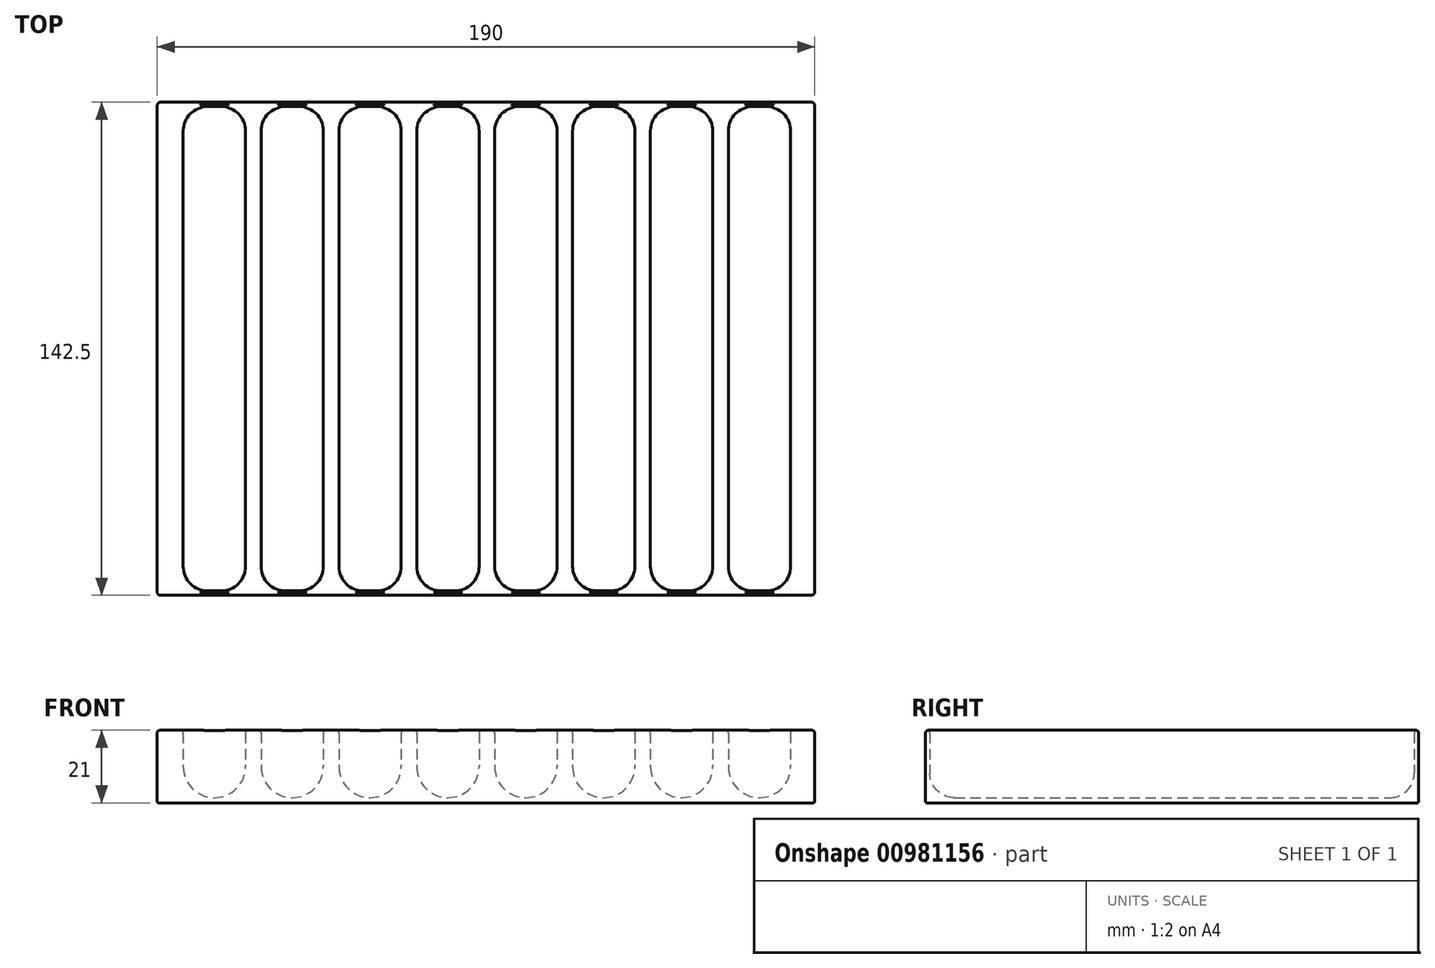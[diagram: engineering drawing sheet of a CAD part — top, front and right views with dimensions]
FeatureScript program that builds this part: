
annotation { "Feature Type Name" : "Feature", "Feature Type Description" : "" }
export const myFeature = defineFeature(function(context is Context, id is Id, definition is map)
    precondition{}
    {
        {
            var Q0;
            Q0=qCreatedBy(makeId("Top.planeOp"),FACE);
            var sketch = newSketch(context, id + "F0", { "sketchPlane" : qUnion([Q0])});
            skLineSegment(sketch, "E0.bottom", {"start": v(95, -71.25) * mm, "end": v(-95, -71.25) * mm});
            skLineSegment(sketch, "E0.top", {"start": v(95, 71.25) * mm, "end": v(-95, 71.25) * mm});
            skLineSegment(sketch, "E0.left", {"start": v(95, -71.25) * mm, "end": v(95, 71.25) * mm});
            skLineSegment(sketch, "E0.right", {"start": v(-95, -71.25) * mm, "end": v(-95, 71.25) * mm});
            skPoint(sketch, "E0.middle", {"position": v(0, 0) * mm});
            skSolve(sketch);
        }
        {
            var Q0;
            Q0 = qSketchRegion(id + "F0", true);
            extrude(context, id + "F1", {"entities" : qUnion([Q0]), "depth" : 21 * mm, "offsetDistance" : 25 * mm});
        }
        {
            var Q0;
            Q0=qCreatedBy(makeId("Front.planeOp"),FACE);
            var sketch = newSketch(context, id + "F2", { "sketchPlane" : qUnion([Q0])});
            skLineSegment(sketch, "E1.bottom", {"start": v(-69.47, 26.52) * mm, "end": v(-87.47, 26.52) * mm});
            skLineSegment(sketch, "E1.top", {"start": v(-69.47, 10.52) * mm, "end": v(-87.47, 10.52) * mm});
            skLineSegment(sketch, "E1.left", {"start": v(-69.47, 26.52) * mm, "end": v(-69.47, 10.52) * mm});
            skLineSegment(sketch, "E1.right", {"start": v(-87.47, 26.52) * mm, "end": v(-87.47, 10.52) * mm});
            skPoint(sketch, "E1.middle", {"position": v(-78.47, 18.52) * mm});
            skArc(sketch, "E2", {"start": v(-87.47, 10.52) * mm, "mid": v(-78.47, 1.52) * mm, "end": v(-69.47, 10.52) * mm});
            skSolve(sketch);
        }
        {
            var Q0;
            Q0=makeQuery(id+"F2.imprint","IMPRINT",FACE,{"disambiguationData":[TD([[makeQuery(id+"F2.imprint","IMPRINT",EDGE,{"derivedFrom":sQuery(id+"F2.wireOp",EDGE,"E1.bottom")}),1.0]])]});
            var Q1;
            Q1=makeQuery(id+"F2.imprint","IMPRINT",FACE,{"disambiguationData":[TD([[makeQuery(id+"F2.imprint","IMPRINT",EDGE,{"derivedFrom":sQuery(id+"F2.wireOp",EDGE,"E1.top")}),1.0]])]});
            extrude(context, id + "F3", {"entities" : qUnion([Q0, Q1]), "depth" : 140 * mm, "offsetDistance" : 25 * mm, "symmetric" : true});
        }
        {
            var Q0;
            Q0=makeQuery(id+"F3.opExtrude","SWEPT_BODY",BODY,{"disambiguationData":[OSD([sQuery(id+"F2.wireOp",EDGE,"E1.bottom"),sQuery(id+"F2.wireOp",EDGE,"E1.left"),sQuery(id+"F2.wireOp",EDGE,"E1.right"),sQuery(id+"F2.wireOp",EDGE,"E2")])]});
            transform(context, id + "F4", {"entities" : qUnion([Q0]), "transformType" : TransformType.TRANSLATION_3D, "dx" : 22.5 * mm, "dy" : 0 * mm, "dz" : 0 * mm, "makeCopy" : true});
        }
        {
            var Q0;
            Q0=makeQuery(id+"F4.opPattern","COPY",BODY,{"derivedFrom":makeQuery(id+"F3.opExtrude","SWEPT_BODY",BODY,{"disambiguationData":[OSD([sQuery(id+"F2.wireOp",EDGE,"E1.bottom"),sQuery(id+"F2.wireOp",EDGE,"E1.left"),sQuery(id+"F2.wireOp",EDGE,"E1.right"),sQuery(id+"F2.wireOp",EDGE,"E2")])]}),"instanceName":"1"});
            transform(context, id + "F5", {"entities" : qUnion([Q0]), "transformType" : TransformType.TRANSLATION_3D, "dx" : 22.5 * mm, "dy" : 0 * mm, "dz" : 0 * mm, "makeCopy" : true});
        }
        {
            var Q0;
            Q0=makeQuery(id+"F5.opPattern","COPY",BODY,{"derivedFrom":makeQuery(id+"F4.opPattern","COPY",BODY,{"derivedFrom":makeQuery(id+"F3.opExtrude","SWEPT_BODY",BODY,{"disambiguationData":[OSD([sQuery(id+"F2.wireOp",EDGE,"E1.bottom"),sQuery(id+"F2.wireOp",EDGE,"E1.left"),sQuery(id+"F2.wireOp",EDGE,"E1.right"),sQuery(id+"F2.wireOp",EDGE,"E2")])]}),"instanceName":"1"}),"instanceName":"1"});
            transform(context, id + "F6", {"entities" : qUnion([Q0]), "transformType" : TransformType.TRANSLATION_3D, "dx" : 22.5 * mm, "dy" : 0 * mm, "dz" : 0 * mm, "makeCopy" : true});
        }
        {
            var Q0;
            Q0=makeQuery(id+"F6.opPattern","COPY",BODY,{"derivedFrom":makeQuery(id+"F5.opPattern","COPY",BODY,{"derivedFrom":makeQuery(id+"F4.opPattern","COPY",BODY,{"derivedFrom":makeQuery(id+"F3.opExtrude","SWEPT_BODY",BODY,{"disambiguationData":[OSD([sQuery(id+"F2.wireOp",EDGE,"E1.bottom"),sQuery(id+"F2.wireOp",EDGE,"E1.left"),sQuery(id+"F2.wireOp",EDGE,"E1.right"),sQuery(id+"F2.wireOp",EDGE,"E2")])]}),"instanceName":"1"}),"instanceName":"1"}),"instanceName":"1"});
            transform(context, id + "F7", {"entities" : qUnion([Q0]), "transformType" : TransformType.TRANSLATION_3D, "dx" : 22.5 * mm, "dy" : 0 * mm, "dz" : 0 * mm, "makeCopy" : true});
        }
        {
            var Q0;
            Q0=makeQuery(id+"F7.opPattern","COPY",BODY,{"derivedFrom":makeQuery(id+"F6.opPattern","COPY",BODY,{"derivedFrom":makeQuery(id+"F5.opPattern","COPY",BODY,{"derivedFrom":makeQuery(id+"F4.opPattern","COPY",BODY,{"derivedFrom":makeQuery(id+"F3.opExtrude","SWEPT_BODY",BODY,{"disambiguationData":[OSD([sQuery(id+"F2.wireOp",EDGE,"E1.bottom"),sQuery(id+"F2.wireOp",EDGE,"E1.left"),sQuery(id+"F2.wireOp",EDGE,"E1.right"),sQuery(id+"F2.wireOp",EDGE,"E2")])]}),"instanceName":"1"}),"instanceName":"1"}),"instanceName":"1"}),"instanceName":"1"});
            transform(context, id + "F8", {"entities" : qUnion([Q0]), "transformType" : TransformType.TRANSLATION_3D, "dx" : 22.5 * mm, "dy" : 0 * mm, "dz" : 0 * mm, "makeCopy" : true});
        }
        {
            var Q0;
            Q0=makeQuery(id+"F8.opPattern","COPY",BODY,{"derivedFrom":makeQuery(id+"F7.opPattern","COPY",BODY,{"derivedFrom":makeQuery(id+"F6.opPattern","COPY",BODY,{"derivedFrom":makeQuery(id+"F5.opPattern","COPY",BODY,{"derivedFrom":makeQuery(id+"F4.opPattern","COPY",BODY,{"derivedFrom":makeQuery(id+"F3.opExtrude","SWEPT_BODY",BODY,{"disambiguationData":[OSD([sQuery(id+"F2.wireOp",EDGE,"E1.bottom"),sQuery(id+"F2.wireOp",EDGE,"E1.left"),sQuery(id+"F2.wireOp",EDGE,"E1.right"),sQuery(id+"F2.wireOp",EDGE,"E2")])]}),"instanceName":"1"}),"instanceName":"1"}),"instanceName":"1"}),"instanceName":"1"}),"instanceName":"1"});
            transform(context, id + "F9", {"entities" : qUnion([Q0]), "transformType" : TransformType.TRANSLATION_3D, "dx" : 22.5 * mm, "dy" : 0 * mm, "dz" : 0 * mm, "makeCopy" : true});
        }
        {
            var Q0;
            Q0=makeQuery(id+"F9.opPattern","COPY",BODY,{"derivedFrom":makeQuery(id+"F8.opPattern","COPY",BODY,{"derivedFrom":makeQuery(id+"F7.opPattern","COPY",BODY,{"derivedFrom":makeQuery(id+"F6.opPattern","COPY",BODY,{"derivedFrom":makeQuery(id+"F5.opPattern","COPY",BODY,{"derivedFrom":makeQuery(id+"F4.opPattern","COPY",BODY,{"derivedFrom":makeQuery(id+"F3.opExtrude","SWEPT_BODY",BODY,{"disambiguationData":[OSD([sQuery(id+"F2.wireOp",EDGE,"E1.bottom"),sQuery(id+"F2.wireOp",EDGE,"E1.left"),sQuery(id+"F2.wireOp",EDGE,"E1.right"),sQuery(id+"F2.wireOp",EDGE,"E2")])]}),"instanceName":"1"}),"instanceName":"1"}),"instanceName":"1"}),"instanceName":"1"}),"instanceName":"1"}),"instanceName":"1"});
            transform(context, id + "F10", {"entities" : qUnion([Q0]), "transformType" : TransformType.TRANSLATION_3D, "dx" : 22.5 * mm, "dy" : 0 * mm, "dz" : 0 * mm, "makeCopy" : true});
        }
        {
            var Q0;
            Q0=makeQuery(id+"F3.opExtrude","SWEPT_BODY",BODY,{"disambiguationData":[OSD([sQuery(id+"F2.wireOp",EDGE,"E1.bottom"),sQuery(id+"F2.wireOp",EDGE,"E1.left"),sQuery(id+"F2.wireOp",EDGE,"E1.right"),sQuery(id+"F2.wireOp",EDGE,"E2")])]});
            var Q1;
            Q1=makeQuery(id+"F4.opPattern","COPY",BODY,{"derivedFrom":makeQuery(id+"F3.opExtrude","SWEPT_BODY",BODY,{"disambiguationData":[OSD([sQuery(id+"F2.wireOp",EDGE,"E1.bottom"),sQuery(id+"F2.wireOp",EDGE,"E1.left"),sQuery(id+"F2.wireOp",EDGE,"E1.right"),sQuery(id+"F2.wireOp",EDGE,"E2")])]}),"instanceName":"1"});
            var Q2;
            Q2=makeQuery(id+"F5.opPattern","COPY",BODY,{"derivedFrom":makeQuery(id+"F4.opPattern","COPY",BODY,{"derivedFrom":makeQuery(id+"F3.opExtrude","SWEPT_BODY",BODY,{"disambiguationData":[OSD([sQuery(id+"F2.wireOp",EDGE,"E1.bottom"),sQuery(id+"F2.wireOp",EDGE,"E1.left"),sQuery(id+"F2.wireOp",EDGE,"E1.right"),sQuery(id+"F2.wireOp",EDGE,"E2")])]}),"instanceName":"1"}),"instanceName":"1"});
            var Q3;
            Q3=makeQuery(id+"F6.opPattern","COPY",BODY,{"derivedFrom":makeQuery(id+"F5.opPattern","COPY",BODY,{"derivedFrom":makeQuery(id+"F4.opPattern","COPY",BODY,{"derivedFrom":makeQuery(id+"F3.opExtrude","SWEPT_BODY",BODY,{"disambiguationData":[OSD([sQuery(id+"F2.wireOp",EDGE,"E1.bottom"),sQuery(id+"F2.wireOp",EDGE,"E1.left"),sQuery(id+"F2.wireOp",EDGE,"E1.right"),sQuery(id+"F2.wireOp",EDGE,"E2")])]}),"instanceName":"1"}),"instanceName":"1"}),"instanceName":"1"});
            var Q4;
            Q4=makeQuery(id+"F7.opPattern","COPY",BODY,{"derivedFrom":makeQuery(id+"F6.opPattern","COPY",BODY,{"derivedFrom":makeQuery(id+"F5.opPattern","COPY",BODY,{"derivedFrom":makeQuery(id+"F4.opPattern","COPY",BODY,{"derivedFrom":makeQuery(id+"F3.opExtrude","SWEPT_BODY",BODY,{"disambiguationData":[OSD([sQuery(id+"F2.wireOp",EDGE,"E1.bottom"),sQuery(id+"F2.wireOp",EDGE,"E1.left"),sQuery(id+"F2.wireOp",EDGE,"E1.right"),sQuery(id+"F2.wireOp",EDGE,"E2")])]}),"instanceName":"1"}),"instanceName":"1"}),"instanceName":"1"}),"instanceName":"1"});
            var Q5;
            Q5=makeQuery(id+"F8.opPattern","COPY",BODY,{"derivedFrom":makeQuery(id+"F7.opPattern","COPY",BODY,{"derivedFrom":makeQuery(id+"F6.opPattern","COPY",BODY,{"derivedFrom":makeQuery(id+"F5.opPattern","COPY",BODY,{"derivedFrom":makeQuery(id+"F4.opPattern","COPY",BODY,{"derivedFrom":makeQuery(id+"F3.opExtrude","SWEPT_BODY",BODY,{"disambiguationData":[OSD([sQuery(id+"F2.wireOp",EDGE,"E1.bottom"),sQuery(id+"F2.wireOp",EDGE,"E1.left"),sQuery(id+"F2.wireOp",EDGE,"E1.right"),sQuery(id+"F2.wireOp",EDGE,"E2")])]}),"instanceName":"1"}),"instanceName":"1"}),"instanceName":"1"}),"instanceName":"1"}),"instanceName":"1"});
            var Q6;
            Q6=makeQuery(id+"F9.opPattern","COPY",BODY,{"derivedFrom":makeQuery(id+"F8.opPattern","COPY",BODY,{"derivedFrom":makeQuery(id+"F7.opPattern","COPY",BODY,{"derivedFrom":makeQuery(id+"F6.opPattern","COPY",BODY,{"derivedFrom":makeQuery(id+"F5.opPattern","COPY",BODY,{"derivedFrom":makeQuery(id+"F4.opPattern","COPY",BODY,{"derivedFrom":makeQuery(id+"F3.opExtrude","SWEPT_BODY",BODY,{"disambiguationData":[OSD([sQuery(id+"F2.wireOp",EDGE,"E1.bottom"),sQuery(id+"F2.wireOp",EDGE,"E1.left"),sQuery(id+"F2.wireOp",EDGE,"E1.right"),sQuery(id+"F2.wireOp",EDGE,"E2")])]}),"instanceName":"1"}),"instanceName":"1"}),"instanceName":"1"}),"instanceName":"1"}),"instanceName":"1"}),"instanceName":"1"});
            var Q7;
            Q7=makeQuery(id+"F10.opPattern","COPY",BODY,{"derivedFrom":makeQuery(id+"F9.opPattern","COPY",BODY,{"derivedFrom":makeQuery(id+"F8.opPattern","COPY",BODY,{"derivedFrom":makeQuery(id+"F7.opPattern","COPY",BODY,{"derivedFrom":makeQuery(id+"F6.opPattern","COPY",BODY,{"derivedFrom":makeQuery(id+"F5.opPattern","COPY",BODY,{"derivedFrom":makeQuery(id+"F4.opPattern","COPY",BODY,{"derivedFrom":makeQuery(id+"F3.opExtrude","SWEPT_BODY",BODY,{"disambiguationData":[OSD([sQuery(id+"F2.wireOp",EDGE,"E1.bottom"),sQuery(id+"F2.wireOp",EDGE,"E1.left"),sQuery(id+"F2.wireOp",EDGE,"E1.right"),sQuery(id+"F2.wireOp",EDGE,"E2")])]}),"instanceName":"1"}),"instanceName":"1"}),"instanceName":"1"}),"instanceName":"1"}),"instanceName":"1"}),"instanceName":"1"}),"instanceName":"1"});
            var Q8;
            Q8=makeQuery(id+"F1.opExtrude","SWEPT_BODY",BODY,{"disambiguationData":[OSD([sQuery(id+"F0.wireOp",EDGE,"E0.bottom"),sQuery(id+"F0.wireOp",EDGE,"E0.top"),sQuery(id+"F0.wireOp",EDGE,"E0.left"),sQuery(id+"F0.wireOp",EDGE,"E0.right")])]});
            booleanBodies(context, id + "F11", {"operationType" : BooleanOperationType.SUBTRACTION, "tools" : qUnion([Q0, Q1, Q2, Q3, Q4, Q5, Q6, Q7]), "targets" : qUnion([Q8])});
        }
        {
            var Q0;
            Q0=makeQuery(id+"F11.opBoolean","COPY",EDGE,{"derivedFrom":makeQuery(id+"F3.opExtrude","CAP_EDGE",EDGE,{"disambiguationData":[OSD([sQuery(id+"F2.wireOp",EDGE,"E2")])],"isStart":true})});
            var Q1;
            Q1=makeQuery(id+"F11.opBoolean","COPY",EDGE,{"derivedFrom":makeQuery(id+"F4.opPattern","COPY",EDGE,{"derivedFrom":makeQuery(id+"F3.opExtrude","CAP_EDGE",EDGE,{"disambiguationData":[OSD([sQuery(id+"F2.wireOp",EDGE,"E2")])],"isStart":true}),"instanceName":"1"})});
            var Q2;
            Q2=makeQuery(id+"F11.opBoolean","COPY",EDGE,{"derivedFrom":makeQuery(id+"F5.opPattern","COPY",EDGE,{"derivedFrom":makeQuery(id+"F4.opPattern","COPY",EDGE,{"derivedFrom":makeQuery(id+"F3.opExtrude","CAP_EDGE",EDGE,{"disambiguationData":[OSD([sQuery(id+"F2.wireOp",EDGE,"E2")])],"isStart":true}),"instanceName":"1"}),"instanceName":"1"})});
            var Q3;
            Q3=makeQuery(id+"F11.opBoolean","COPY",EDGE,{"derivedFrom":makeQuery(id+"F6.opPattern","COPY",EDGE,{"derivedFrom":makeQuery(id+"F5.opPattern","COPY",EDGE,{"derivedFrom":makeQuery(id+"F4.opPattern","COPY",EDGE,{"derivedFrom":makeQuery(id+"F3.opExtrude","CAP_EDGE",EDGE,{"disambiguationData":[OSD([sQuery(id+"F2.wireOp",EDGE,"E2")])],"isStart":true}),"instanceName":"1"}),"instanceName":"1"}),"instanceName":"1"})});
            var Q4;
            Q4=makeQuery(id+"F11.opBoolean","COPY",EDGE,{"derivedFrom":makeQuery(id+"F8.opPattern","COPY",EDGE,{"derivedFrom":makeQuery(id+"F7.opPattern","COPY",EDGE,{"derivedFrom":makeQuery(id+"F6.opPattern","COPY",EDGE,{"derivedFrom":makeQuery(id+"F5.opPattern","COPY",EDGE,{"derivedFrom":makeQuery(id+"F4.opPattern","COPY",EDGE,{"derivedFrom":makeQuery(id+"F3.opExtrude","CAP_EDGE",EDGE,{"disambiguationData":[OSD([sQuery(id+"F2.wireOp",EDGE,"E2")])],"isStart":true}),"instanceName":"1"}),"instanceName":"1"}),"instanceName":"1"}),"instanceName":"1"}),"instanceName":"1"})});
            var Q5;
            Q5=makeQuery(id+"F11.opBoolean","COPY",EDGE,{"derivedFrom":makeQuery(id+"F7.opPattern","COPY",EDGE,{"derivedFrom":makeQuery(id+"F6.opPattern","COPY",EDGE,{"derivedFrom":makeQuery(id+"F5.opPattern","COPY",EDGE,{"derivedFrom":makeQuery(id+"F4.opPattern","COPY",EDGE,{"derivedFrom":makeQuery(id+"F3.opExtrude","CAP_EDGE",EDGE,{"disambiguationData":[OSD([sQuery(id+"F2.wireOp",EDGE,"E2")])],"isStart":true}),"instanceName":"1"}),"instanceName":"1"}),"instanceName":"1"}),"instanceName":"1"})});
            var Q6;
            Q6=makeQuery(id+"F11.opBoolean","COPY",EDGE,{"derivedFrom":makeQuery(id+"F9.opPattern","COPY",EDGE,{"derivedFrom":makeQuery(id+"F8.opPattern","COPY",EDGE,{"derivedFrom":makeQuery(id+"F7.opPattern","COPY",EDGE,{"derivedFrom":makeQuery(id+"F6.opPattern","COPY",EDGE,{"derivedFrom":makeQuery(id+"F5.opPattern","COPY",EDGE,{"derivedFrom":makeQuery(id+"F4.opPattern","COPY",EDGE,{"derivedFrom":makeQuery(id+"F3.opExtrude","CAP_EDGE",EDGE,{"disambiguationData":[OSD([sQuery(id+"F2.wireOp",EDGE,"E2")])],"isStart":true}),"instanceName":"1"}),"instanceName":"1"}),"instanceName":"1"}),"instanceName":"1"}),"instanceName":"1"}),"instanceName":"1"})});
            var Q7;
            Q7=makeQuery(id+"F11.opBoolean","COPY",EDGE,{"derivedFrom":makeQuery(id+"F10.opPattern","COPY",EDGE,{"derivedFrom":makeQuery(id+"F9.opPattern","COPY",EDGE,{"derivedFrom":makeQuery(id+"F8.opPattern","COPY",EDGE,{"derivedFrom":makeQuery(id+"F7.opPattern","COPY",EDGE,{"derivedFrom":makeQuery(id+"F6.opPattern","COPY",EDGE,{"derivedFrom":makeQuery(id+"F5.opPattern","COPY",EDGE,{"derivedFrom":makeQuery(id+"F4.opPattern","COPY",EDGE,{"derivedFrom":makeQuery(id+"F3.opExtrude","CAP_EDGE",EDGE,{"disambiguationData":[OSD([sQuery(id+"F2.wireOp",EDGE,"E2")])],"isStart":true}),"instanceName":"1"}),"instanceName":"1"}),"instanceName":"1"}),"instanceName":"1"}),"instanceName":"1"}),"instanceName":"1"}),"instanceName":"1"})});
            var Q8;
            Q8=makeQuery(id+"F11.opBoolean","COPY",EDGE,{"derivedFrom":makeQuery(id+"F10.opPattern","COPY",EDGE,{"derivedFrom":makeQuery(id+"F9.opPattern","COPY",EDGE,{"derivedFrom":makeQuery(id+"F8.opPattern","COPY",EDGE,{"derivedFrom":makeQuery(id+"F7.opPattern","COPY",EDGE,{"derivedFrom":makeQuery(id+"F6.opPattern","COPY",EDGE,{"derivedFrom":makeQuery(id+"F5.opPattern","COPY",EDGE,{"derivedFrom":makeQuery(id+"F4.opPattern","COPY",EDGE,{"derivedFrom":makeQuery(id+"F3.opExtrude","CAP_EDGE",EDGE,{"disambiguationData":[OSD([sQuery(id+"F2.wireOp",EDGE,"E2")])],"isStart":false}),"instanceName":"1"}),"instanceName":"1"}),"instanceName":"1"}),"instanceName":"1"}),"instanceName":"1"}),"instanceName":"1"}),"instanceName":"1"})});
            var Q9;
            Q9=makeQuery(id+"F11.opBoolean","COPY",EDGE,{"derivedFrom":makeQuery(id+"F9.opPattern","COPY",EDGE,{"derivedFrom":makeQuery(id+"F8.opPattern","COPY",EDGE,{"derivedFrom":makeQuery(id+"F7.opPattern","COPY",EDGE,{"derivedFrom":makeQuery(id+"F6.opPattern","COPY",EDGE,{"derivedFrom":makeQuery(id+"F5.opPattern","COPY",EDGE,{"derivedFrom":makeQuery(id+"F4.opPattern","COPY",EDGE,{"derivedFrom":makeQuery(id+"F3.opExtrude","CAP_EDGE",EDGE,{"disambiguationData":[OSD([sQuery(id+"F2.wireOp",EDGE,"E2")])],"isStart":false}),"instanceName":"1"}),"instanceName":"1"}),"instanceName":"1"}),"instanceName":"1"}),"instanceName":"1"}),"instanceName":"1"})});
            var Q10;
            Q10=makeQuery(id+"F11.opBoolean","COPY",EDGE,{"derivedFrom":makeQuery(id+"F8.opPattern","COPY",EDGE,{"derivedFrom":makeQuery(id+"F7.opPattern","COPY",EDGE,{"derivedFrom":makeQuery(id+"F6.opPattern","COPY",EDGE,{"derivedFrom":makeQuery(id+"F5.opPattern","COPY",EDGE,{"derivedFrom":makeQuery(id+"F4.opPattern","COPY",EDGE,{"derivedFrom":makeQuery(id+"F3.opExtrude","CAP_EDGE",EDGE,{"disambiguationData":[OSD([sQuery(id+"F2.wireOp",EDGE,"E2")])],"isStart":false}),"instanceName":"1"}),"instanceName":"1"}),"instanceName":"1"}),"instanceName":"1"}),"instanceName":"1"})});
            var Q11;
            Q11=makeQuery(id+"F11.opBoolean","COPY",EDGE,{"derivedFrom":makeQuery(id+"F7.opPattern","COPY",EDGE,{"derivedFrom":makeQuery(id+"F6.opPattern","COPY",EDGE,{"derivedFrom":makeQuery(id+"F5.opPattern","COPY",EDGE,{"derivedFrom":makeQuery(id+"F4.opPattern","COPY",EDGE,{"derivedFrom":makeQuery(id+"F3.opExtrude","CAP_EDGE",EDGE,{"disambiguationData":[OSD([sQuery(id+"F2.wireOp",EDGE,"E2")])],"isStart":false}),"instanceName":"1"}),"instanceName":"1"}),"instanceName":"1"}),"instanceName":"1"})});
            var Q12;
            Q12=makeQuery(id+"F11.opBoolean","COPY",EDGE,{"derivedFrom":makeQuery(id+"F6.opPattern","COPY",EDGE,{"derivedFrom":makeQuery(id+"F5.opPattern","COPY",EDGE,{"derivedFrom":makeQuery(id+"F4.opPattern","COPY",EDGE,{"derivedFrom":makeQuery(id+"F3.opExtrude","CAP_EDGE",EDGE,{"disambiguationData":[OSD([sQuery(id+"F2.wireOp",EDGE,"E2")])],"isStart":false}),"instanceName":"1"}),"instanceName":"1"}),"instanceName":"1"})});
            var Q13;
            Q13=makeQuery(id+"F11.opBoolean","COPY",EDGE,{"derivedFrom":makeQuery(id+"F5.opPattern","COPY",EDGE,{"derivedFrom":makeQuery(id+"F4.opPattern","COPY",EDGE,{"derivedFrom":makeQuery(id+"F3.opExtrude","CAP_EDGE",EDGE,{"disambiguationData":[OSD([sQuery(id+"F2.wireOp",EDGE,"E2")])],"isStart":false}),"instanceName":"1"}),"instanceName":"1"})});
            var Q14;
            Q14=makeQuery(id+"F11.opBoolean","COPY",EDGE,{"derivedFrom":makeQuery(id+"F4.opPattern","COPY",EDGE,{"derivedFrom":makeQuery(id+"F3.opExtrude","CAP_EDGE",EDGE,{"disambiguationData":[OSD([sQuery(id+"F2.wireOp",EDGE,"E2")])],"isStart":false}),"instanceName":"1"})});
            var Q15;
            Q15=makeQuery(id+"F11.opBoolean","COPY",EDGE,{"derivedFrom":makeQuery(id+"F3.opExtrude","CAP_EDGE",EDGE,{"disambiguationData":[OSD([sQuery(id+"F2.wireOp",EDGE,"E2")])],"isStart":false})});
            fillet(context, id + "F12", {"entities" : qUnion([Q0, Q1, Q2, Q3, Q4, Q5, Q6, Q7, Q8, Q9, Q10, Q11, Q12, Q13, Q14, Q15]), "tangentPropagation" : true, "radius" : 7.1 * mm, "defaultsChanged" : true, "vertexSettings" : [], "allowEdgeOverflow" : false});
        }
        {
            var Q0;
            Q0=makeQuery(id+"F11.opBoolean","INTERSECT",EDGE,{"derivedFrom":[makeQuery(id+"F1.opExtrude","CAP_FACE",FACE,{"disambiguationData":[OSD([sQuery(id+"F0.wireOp",EDGE,"E0.bottom"),sQuery(id+"F0.wireOp",EDGE,"E0.top"),sQuery(id+"F0.wireOp",EDGE,"E0.left"),sQuery(id+"F0.wireOp",EDGE,"E0.right")])],"isStart":false}),makeQuery(id+"F3.opExtrude","SWEPT_FACE",FACE,{"disambiguationData":[OSD([sQuery(id+"F2.wireOp",EDGE,"E1.right")])]})]});
            var Q1;
            Q1=makeQuery(id+"F11.opBoolean","INTERSECT",EDGE,{"derivedFrom":[makeQuery(id+"F1.opExtrude","CAP_FACE",FACE,{"disambiguationData":[OSD([sQuery(id+"F0.wireOp",EDGE,"E0.bottom"),sQuery(id+"F0.wireOp",EDGE,"E0.top"),sQuery(id+"F0.wireOp",EDGE,"E0.left"),sQuery(id+"F0.wireOp",EDGE,"E0.right")])],"isStart":false}),makeQuery(id+"F4.opPattern","COPY",FACE,{"derivedFrom":makeQuery(id+"F3.opExtrude","SWEPT_FACE",FACE,{"disambiguationData":[OSD([sQuery(id+"F2.wireOp",EDGE,"E1.right")])]}),"instanceName":"1"})]});
            var Q2;
            Q2=makeQuery(id+"F11.opBoolean","INTERSECT",EDGE,{"derivedFrom":[makeQuery(id+"F1.opExtrude","CAP_FACE",FACE,{"disambiguationData":[OSD([sQuery(id+"F0.wireOp",EDGE,"E0.bottom"),sQuery(id+"F0.wireOp",EDGE,"E0.top"),sQuery(id+"F0.wireOp",EDGE,"E0.left"),sQuery(id+"F0.wireOp",EDGE,"E0.right")])],"isStart":false}),makeQuery(id+"F5.opPattern","COPY",FACE,{"derivedFrom":makeQuery(id+"F4.opPattern","COPY",FACE,{"derivedFrom":makeQuery(id+"F3.opExtrude","SWEPT_FACE",FACE,{"disambiguationData":[OSD([sQuery(id+"F2.wireOp",EDGE,"E1.right")])]}),"instanceName":"1"}),"instanceName":"1"})]});
            var Q3;
            Q3=makeQuery(id+"F11.opBoolean","INTERSECT",EDGE,{"derivedFrom":[makeQuery(id+"F1.opExtrude","CAP_FACE",FACE,{"disambiguationData":[OSD([sQuery(id+"F0.wireOp",EDGE,"E0.bottom"),sQuery(id+"F0.wireOp",EDGE,"E0.top"),sQuery(id+"F0.wireOp",EDGE,"E0.left"),sQuery(id+"F0.wireOp",EDGE,"E0.right")])],"isStart":false}),makeQuery(id+"F6.opPattern","COPY",FACE,{"derivedFrom":makeQuery(id+"F5.opPattern","COPY",FACE,{"derivedFrom":makeQuery(id+"F4.opPattern","COPY",FACE,{"derivedFrom":makeQuery(id+"F3.opExtrude","SWEPT_FACE",FACE,{"disambiguationData":[OSD([sQuery(id+"F2.wireOp",EDGE,"E1.right")])]}),"instanceName":"1"}),"instanceName":"1"}),"instanceName":"1"})]});
            var Q4;
            Q4=makeQuery(id+"F11.opBoolean","INTERSECT",EDGE,{"derivedFrom":[makeQuery(id+"F1.opExtrude","CAP_FACE",FACE,{"disambiguationData":[OSD([sQuery(id+"F0.wireOp",EDGE,"E0.bottom"),sQuery(id+"F0.wireOp",EDGE,"E0.top"),sQuery(id+"F0.wireOp",EDGE,"E0.left"),sQuery(id+"F0.wireOp",EDGE,"E0.right")])],"isStart":false}),makeQuery(id+"F7.opPattern","COPY",FACE,{"derivedFrom":makeQuery(id+"F6.opPattern","COPY",FACE,{"derivedFrom":makeQuery(id+"F5.opPattern","COPY",FACE,{"derivedFrom":makeQuery(id+"F4.opPattern","COPY",FACE,{"derivedFrom":makeQuery(id+"F3.opExtrude","SWEPT_FACE",FACE,{"disambiguationData":[OSD([sQuery(id+"F2.wireOp",EDGE,"E1.right")])]}),"instanceName":"1"}),"instanceName":"1"}),"instanceName":"1"}),"instanceName":"1"})]});
            var Q5;
            Q5=makeQuery(id+"F11.opBoolean","INTERSECT",EDGE,{"derivedFrom":[makeQuery(id+"F1.opExtrude","CAP_FACE",FACE,{"disambiguationData":[OSD([sQuery(id+"F0.wireOp",EDGE,"E0.bottom"),sQuery(id+"F0.wireOp",EDGE,"E0.top"),sQuery(id+"F0.wireOp",EDGE,"E0.left"),sQuery(id+"F0.wireOp",EDGE,"E0.right")])],"isStart":false}),makeQuery(id+"F8.opPattern","COPY",FACE,{"derivedFrom":makeQuery(id+"F7.opPattern","COPY",FACE,{"derivedFrom":makeQuery(id+"F6.opPattern","COPY",FACE,{"derivedFrom":makeQuery(id+"F5.opPattern","COPY",FACE,{"derivedFrom":makeQuery(id+"F4.opPattern","COPY",FACE,{"derivedFrom":makeQuery(id+"F3.opExtrude","SWEPT_FACE",FACE,{"disambiguationData":[OSD([sQuery(id+"F2.wireOp",EDGE,"E1.right")])]}),"instanceName":"1"}),"instanceName":"1"}),"instanceName":"1"}),"instanceName":"1"}),"instanceName":"1"})]});
            var Q6;
            Q6=makeQuery(id+"F11.opBoolean","INTERSECT",EDGE,{"derivedFrom":[makeQuery(id+"F1.opExtrude","CAP_FACE",FACE,{"disambiguationData":[OSD([sQuery(id+"F0.wireOp",EDGE,"E0.bottom"),sQuery(id+"F0.wireOp",EDGE,"E0.top"),sQuery(id+"F0.wireOp",EDGE,"E0.left"),sQuery(id+"F0.wireOp",EDGE,"E0.right")])],"isStart":false}),makeQuery(id+"F9.opPattern","COPY",FACE,{"derivedFrom":makeQuery(id+"F8.opPattern","COPY",FACE,{"derivedFrom":makeQuery(id+"F7.opPattern","COPY",FACE,{"derivedFrom":makeQuery(id+"F6.opPattern","COPY",FACE,{"derivedFrom":makeQuery(id+"F5.opPattern","COPY",FACE,{"derivedFrom":makeQuery(id+"F4.opPattern","COPY",FACE,{"derivedFrom":makeQuery(id+"F3.opExtrude","SWEPT_FACE",FACE,{"disambiguationData":[OSD([sQuery(id+"F2.wireOp",EDGE,"E1.right")])]}),"instanceName":"1"}),"instanceName":"1"}),"instanceName":"1"}),"instanceName":"1"}),"instanceName":"1"}),"instanceName":"1"})]});
            var Q7;
            Q7=makeQuery(id+"F11.opBoolean","INTERSECT",EDGE,{"derivedFrom":[makeQuery(id+"F1.opExtrude","CAP_FACE",FACE,{"disambiguationData":[OSD([sQuery(id+"F0.wireOp",EDGE,"E0.bottom"),sQuery(id+"F0.wireOp",EDGE,"E0.top"),sQuery(id+"F0.wireOp",EDGE,"E0.left"),sQuery(id+"F0.wireOp",EDGE,"E0.right")])],"isStart":false}),makeQuery(id+"F10.opPattern","COPY",FACE,{"derivedFrom":makeQuery(id+"F9.opPattern","COPY",FACE,{"derivedFrom":makeQuery(id+"F8.opPattern","COPY",FACE,{"derivedFrom":makeQuery(id+"F7.opPattern","COPY",FACE,{"derivedFrom":makeQuery(id+"F6.opPattern","COPY",FACE,{"derivedFrom":makeQuery(id+"F5.opPattern","COPY",FACE,{"derivedFrom":makeQuery(id+"F4.opPattern","COPY",FACE,{"derivedFrom":makeQuery(id+"F3.opExtrude","SWEPT_FACE",FACE,{"disambiguationData":[OSD([sQuery(id+"F2.wireOp",EDGE,"E1.right")])]}),"instanceName":"1"}),"instanceName":"1"}),"instanceName":"1"}),"instanceName":"1"}),"instanceName":"1"}),"instanceName":"1"}),"instanceName":"1"})]});
            var Q8;
            Q8=makeQuery(id+"F1.opExtrude","CAP_EDGE",EDGE,{"disambiguationData":[OSD([sQuery(id+"F0.wireOp",EDGE,"E0.right")])],"isStart":false});
            var Q9;
            Q9=makeQuery(id+"F1.opExtrude","CAP_EDGE",EDGE,{"disambiguationData":[OSD([sQuery(id+"F0.wireOp",EDGE,"E0.bottom")])],"isStart":false});
            var Q10;
            Q10=makeQuery(id+"F1.opExtrude","CAP_EDGE",EDGE,{"disambiguationData":[OSD([sQuery(id+"F0.wireOp",EDGE,"E0.left")])],"isStart":false});
            var Q11;
            Q11=makeQuery(id+"F1.opExtrude","CAP_EDGE",EDGE,{"disambiguationData":[OSD([sQuery(id+"F0.wireOp",EDGE,"E0.top")])],"isStart":false});
            fillet(context, id + "F13", {"entities" : qUnion([Q0, Q1, Q2, Q3, Q4, Q5, Q6, Q7, Q8, Q9, Q10, Q11]), "tangentPropagation" : true, "radius" : .8 * mm, "defaultsChanged" : false, "vertexSettings" : [], "allowEdgeOverflow" : false});
        }
        {
            var Q0;
            Q0=makeQuery(id+"F1.opExtrude","SWEPT_EDGE",EDGE,{"disambiguationData":[OSD([sQuery(id+"F0.wireOp",EDGE,"E0.bottom"),sQuery(id+"F0.wireOp",EDGE,"E0.right")])]});
            var Q1;
            Q1=makeQuery(id+"F1.opExtrude","SWEPT_EDGE",EDGE,{"disambiguationData":[OSD([sQuery(id+"F0.wireOp",EDGE,"E0.top"),sQuery(id+"F0.wireOp",EDGE,"E0.right")])]});
            var Q2;
            Q2=makeQuery(id+"F1.opExtrude","SWEPT_EDGE",EDGE,{"disambiguationData":[OSD([sQuery(id+"F0.wireOp",EDGE,"E0.bottom"),sQuery(id+"F0.wireOp",EDGE,"E0.left")])]});
            var Q3;
            Q3=makeQuery(id+"F1.opExtrude","SWEPT_EDGE",EDGE,{"disambiguationData":[OSD([sQuery(id+"F0.wireOp",EDGE,"E0.top"),sQuery(id+"F0.wireOp",EDGE,"E0.left")])]});
            fillet(context, id + "F14", {"entities" : qUnion([Q0, Q1, Q2, Q3]), "tangentPropagation" : true, "radius" : 1 * mm, "defaultsChanged" : false, "vertexSettings" : [], "allowEdgeOverflow" : false});
        }
        {
            var Q0;
            Q0=makeQuery(id+"F1.opExtrude","CAP_FACE",FACE,{"disambiguationData":[OSD([sQuery(id+"F0.wireOp",EDGE,"E0.bottom"),sQuery(id+"F0.wireOp",EDGE,"E0.top"),sQuery(id+"F0.wireOp",EDGE,"E0.left"),sQuery(id+"F0.wireOp",EDGE,"E0.right")])],"isStart":true});
            fillet(context, id + "F15", {"entities" : qUnion([Q0]), "tangentPropagation" : true, "radius" : .5 * mm, "defaultsChanged" : false, "vertexSettings" : [], "allowEdgeOverflow" : false});
        }
    });
